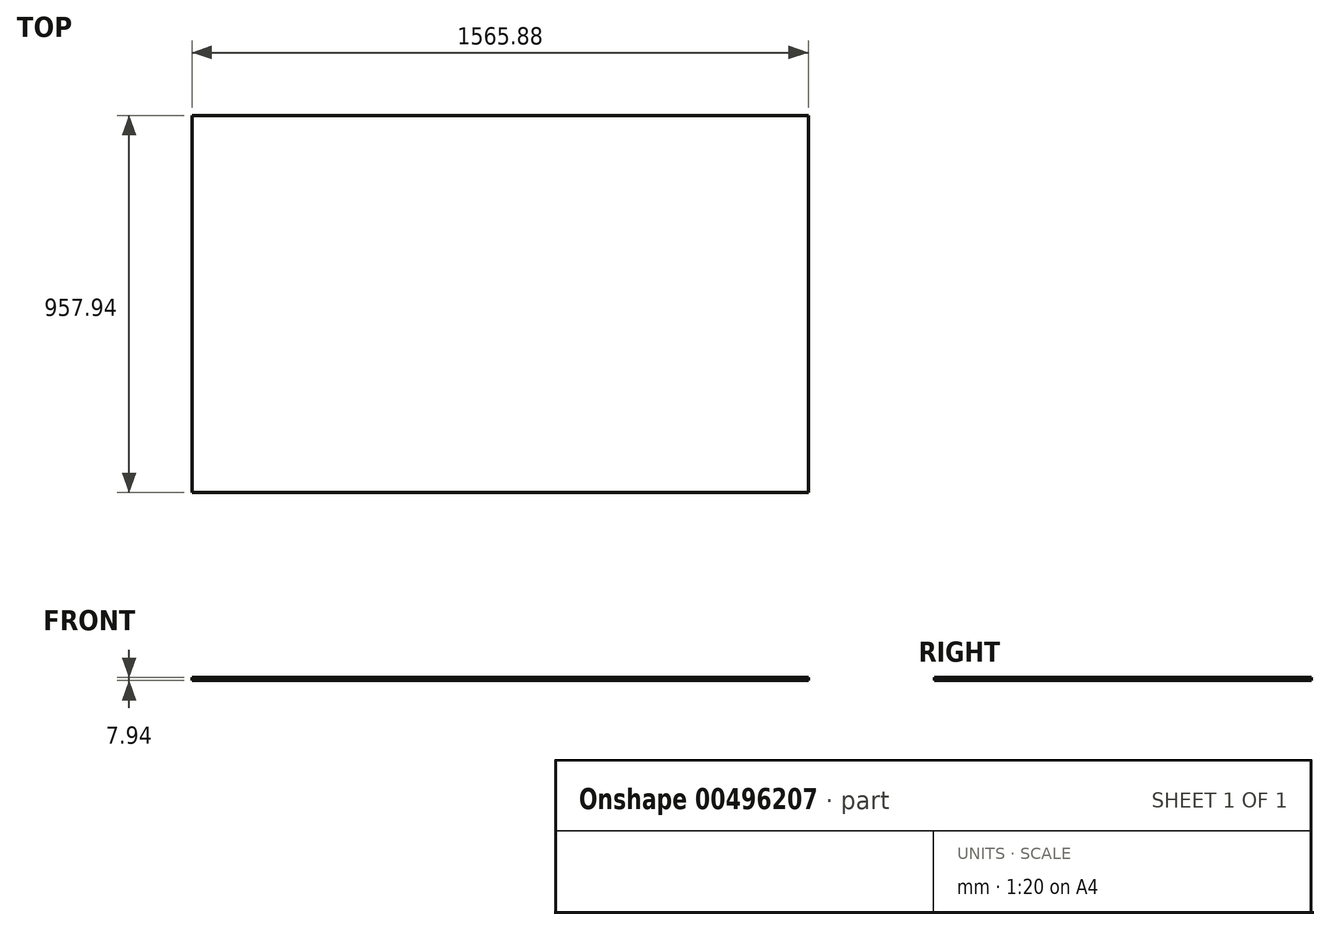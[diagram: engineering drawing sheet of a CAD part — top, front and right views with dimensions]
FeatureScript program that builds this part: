
annotation { "Feature Type Name" : "Feature", "Feature Type Description" : "" }
export const myFeature = defineFeature(function(context is Context, id is Id, definition is map)
    precondition{}
    {
        {
            var Q0;
            Q0=qCreatedBy(makeId("Top.planeOp"),FACE);
            var sketch = newSketch(context, id + "F0", { "sketchPlane" : qUnion([Q0])});
            skLineSegment(sketch, "E0.bottom", {"start": v(-782.94, 0) * mm, "end": v(782.94, 0) * mm});
            skLineSegment(sketch, "E0.top", {"start": v(-782.94, -957.94) * mm, "end": v(782.94, -957.94) * mm});
            skLineSegment(sketch, "E0.left", {"start": v(-782.94, 0) * mm, "end": v(-782.94, -957.94) * mm});
            skLineSegment(sketch, "E0.right", {"start": v(782.94, 0) * mm, "end": v(782.94, -957.94) * mm});
            skSolve(sketch);
        }
        {
            var Q0;
            Q0 = qSketchRegion(id + "F0", true);
            extrude(context, id + "F1", {"entities" : qUnion([Q0]), "depth" : 7.94 * mm, "offsetDistance" : 25.4 * mm});
        }
    });
